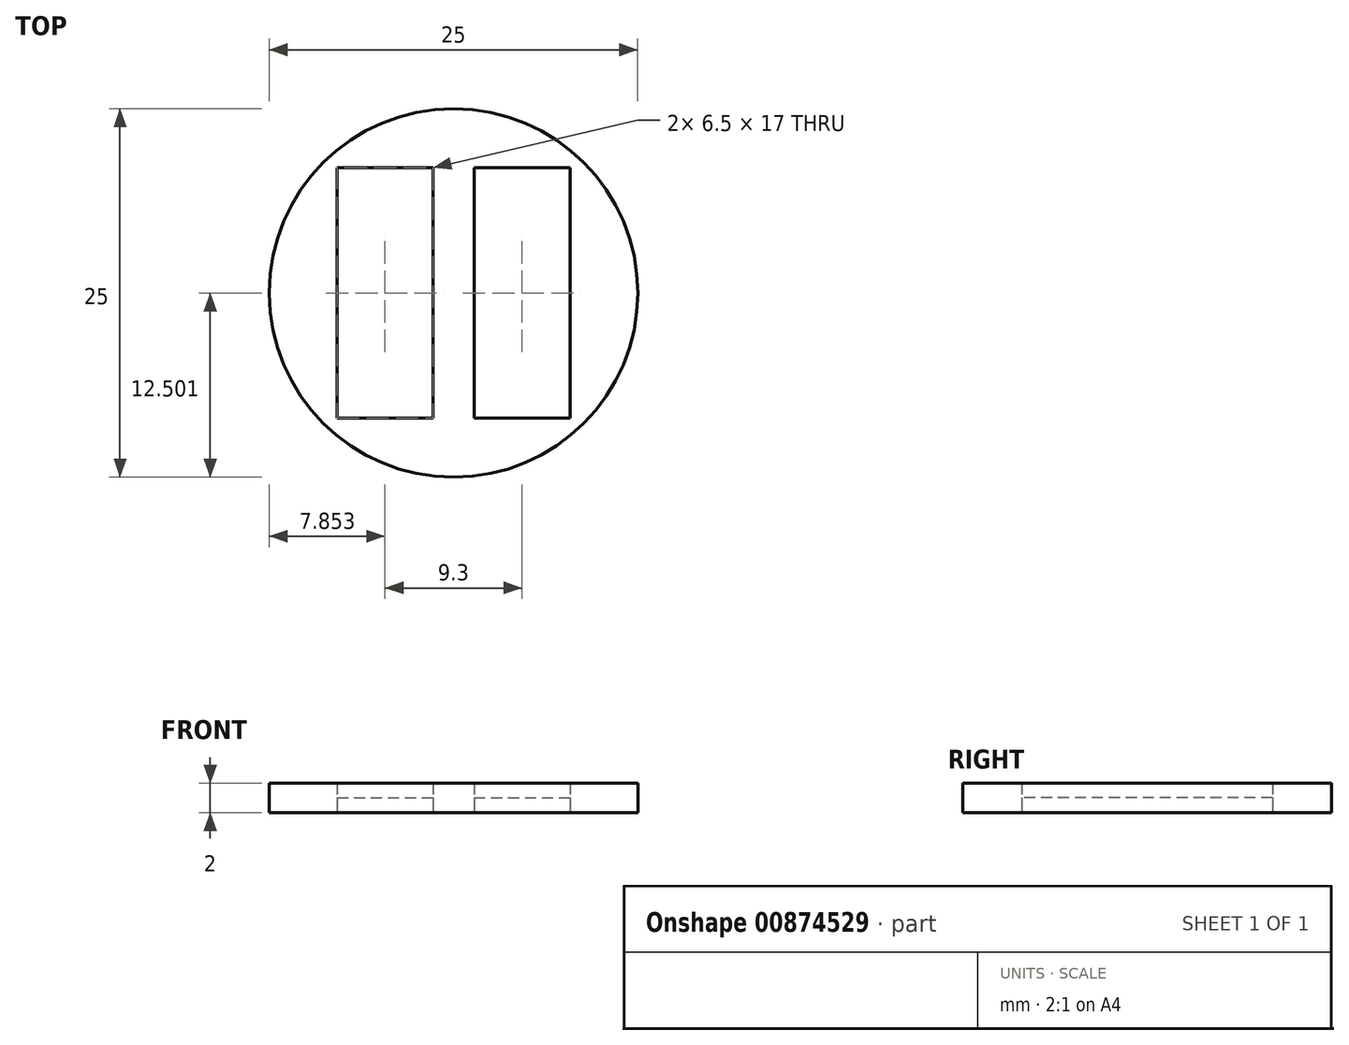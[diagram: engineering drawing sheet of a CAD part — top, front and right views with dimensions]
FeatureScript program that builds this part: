
annotation { "Feature Type Name" : "Feature", "Feature Type Description" : "" }
export const myFeature = defineFeature(function(context is Context, id is Id, definition is map)
    precondition{}
    {
        {
            var Q0;
            Q0=qCreatedBy(makeId("Top.planeOp"),FACE);
            var sketch = newSketch(context, id + "F0", { "sketchPlane" : qUnion([Q0])});
            skCircle(sketch, "E0", {"center": v(11.28, -10.72) * mm, "radius": 12.5 * mm});
            skLineSegment(sketch, "E1.bottom", {"start": v(3.38, -2.22) * mm, "end": v(9.88, -2.22) * mm});
            skLineSegment(sketch, "E1.top", {"start": v(3.38, -19.22) * mm, "end": v(9.88, -19.22) * mm});
            skLineSegment(sketch, "E1.left", {"start": v(3.38, -2.22) * mm, "end": v(3.38, -19.22) * mm});
            skLineSegment(sketch, "E1.right", {"start": v(9.88, -2.22) * mm, "end": v(9.88, -19.22) * mm});
            skLineSegment(sketch, "E2.bottom", {"start": v(12.68, -2.22) * mm, "end": v(19.18, -2.22) * mm});
            skLineSegment(sketch, "E2.top", {"start": v(12.68, -19.22) * mm, "end": v(19.18, -19.22) * mm});
            skLineSegment(sketch, "E2.left", {"start": v(12.68, -2.22) * mm, "end": v(12.68, -19.22) * mm});
            skLineSegment(sketch, "E2.right", {"start": v(19.18, -2.22) * mm, "end": v(19.18, -19.22) * mm});
            skSolve(sketch);
        }
        {
            var Q0;
            Q0=makeQuery(id+"F0.imprint","IMPRINT",FACE,{"disambiguationData":[TD([[makeQuery(id+"F0.imprint","IMPRINT",EDGE,{"derivedFrom":sQuery(id+"F0.wireOp",EDGE,"E1.bottom")}),-1.0]])]});
            var Q1;
            Q1=makeQuery(id+"F0.imprint","IMPRINT",FACE,{"disambiguationData":[TD([[makeQuery(id+"F0.imprint","IMPRINT",EDGE,{"derivedFrom":sQuery(id+"F0.wireOp",EDGE,"E2.bottom")}),-1.0]])]});
            extrude(context, id + "F1", {"entities" : qUnion([Q0, Q1]), "depth" : 1 * mm, "offsetDistance" : 25 * mm});
        }
        {
            var Q0;
            Q0 = qSketchRegion(id + "F0", true);
            extrude(context, id + "F2", {"entities" : qUnion([Q0]), "depth" : 2 * mm, "offsetDistance" : 25 * mm});
        }
    });
